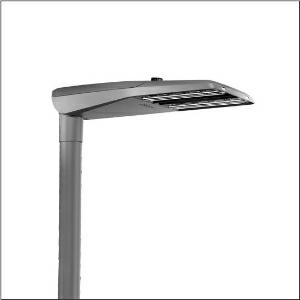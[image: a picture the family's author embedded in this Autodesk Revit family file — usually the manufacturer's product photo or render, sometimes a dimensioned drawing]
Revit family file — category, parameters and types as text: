
# Revit family: streetlight_sl_11_iq_midi___st1_2a_5xc3a41u08le_6743
name_source: partatom
category: Lighting Fixtures
units: mm (PartAtom-declared; Revit-internal decimal feet)

## family parameters
Cut with Voids When Loaded = No
Host = Face
Light Source = No
Part Type = Normal
Room Calculation Point = No
Round Connector Dimension = Use Diameter
Shared = No

## types (1)
- --- (1 x LED, 9590 lm, 59.4 W, 4000K)
    Apparent Load = 59 VA
    CIE Flux Codes = 32 70 96 100 100
    Color Rendering = 70
    Color Temperature = 4000K
    Default Elevation = 1800 mm
    Description = Streetlight SL 11 iQ midi, mast luminaire, primary light control with 3 zone facetted reflector, of plastic, silver coated, highly specular, primary optical cover: cover, of PMMA, transparent, light distribution: ST1.2a, light emission: direct distribution, primary light characteristic: asymmetric, installation type: post-top, side-entry, lamps: LED, High Power LED, rated values: 9.590lm | 59,4W | 161,4lm/W (begin service life); end service life: 9.590lm | 61,6W; at 50% lumin. flux: 4.795lm | 28,5W | 168,2lm/W, colour temperature: 4000K, colour rendering: CRI > 70, light colour: 740, light setting 1 begin service life: 100% | 9.590lm | 59,4W | 161,4lm/W | 4.000K, light setting 1 end service life: 61,6W, further light settings possible, control: pre-setting: logarithmic dimming characteristic, Street-Remote, Auto-Match, Temp-Guard, Lumen-Switch, Night-Set, Smart-Wire, Light-Fading, Desk-Remote (wireless, voltage-free reading and setting of iQ features in the workshop via application-optimized NFC function/RFID function), optimised constant luminous flux control (CLO 2.0), with cable H07RN-F 5x 1.5mm², mains connection: 230..240V, AC, 50/60Hz, connection cable pre-assembled, cable length: 8,5m, luminaire housing, of diecast aluminium, powder-coated, Siteco® metallic grey (DB 702S), please order mast flange separately, inclination adjustable without tools: 0°, 5°, 10°, 15° (post-top) | 0°, -5°, -10°, -15° (side-entry), sealing non-destructively replaceable, multi-level sealing system, length: 780mm, width: 376mm, height: 118mm, mast flange for spigot size: 42mm (side-entry): 5XC10008XM4, 60/48mm (side-entry/post-top): 5XC10108XM2, 76/60mm (side-entry/post-top): 5XC10108XM1, equipment: standard, Smart Interface below, protection rating (complete): IP66, insulation class (complete): insulation class II (safety insulation), certification: CE, ENEC, ENEC+, VDE, UKCA, impact resistance: IK10, permissible operating ambient temperature for outdoor applications: -25..+50°C, standard-compliant lighting for roads and squares, Environmental Product Declaration (EPD) tested and certified by an independent institute, packaging unit: 1 piece

Light Distribution: ST1.2a
    Height = 118 mm
    Lamp = 1 x LED
    Lamp Light Flux = 9590 lm
    Lamp Power = 59.4 W
    Lamp count = 1
    Length = 780 mm
    Luminous efficacy = 161 lm/W
    Manufacturer = Siteco
    ModVariant = No
    Model = 5XC3A41U08LE
    Number of Poles = 1
    OnlyDefault = Yes
    Power Factor = 1
    Product Name = Streetlight SL 11 iQ midi | ST1.2a
    Product group = mast luminaire | pylon top
    ProductGroupID = 6100
    Protection Class = Protection class II
    Protection Degree = IP 66
    RLX_Detail_Level = 1
    RLX_Emergency_Light_Flux = 0 lm
    RLX_Emergency_Type = 0
    RLX_Emergency_Type_DB = No
    RlxData = <blob elided: 69857 chars, md5=24f1a36a>
    Socket = socket
    Standby Power = 0 W
    System Light Flux = 9590 lm
    System Power = 59 W
    Type Comments = factory setting: luminous flux: 100 % | dim-lin: 254 | 521 mA
    Type Image = l_1005968.jpg
    URL = http://relux.com
    VarID = @adj_154593
    Voltage = 0 V
    Weight = 0.00 kg
    Width = 376 mm

## geometry (parser evidence)
native form markers: Blend x4, Sweep x9
no freeform markers — native parametric forms only
